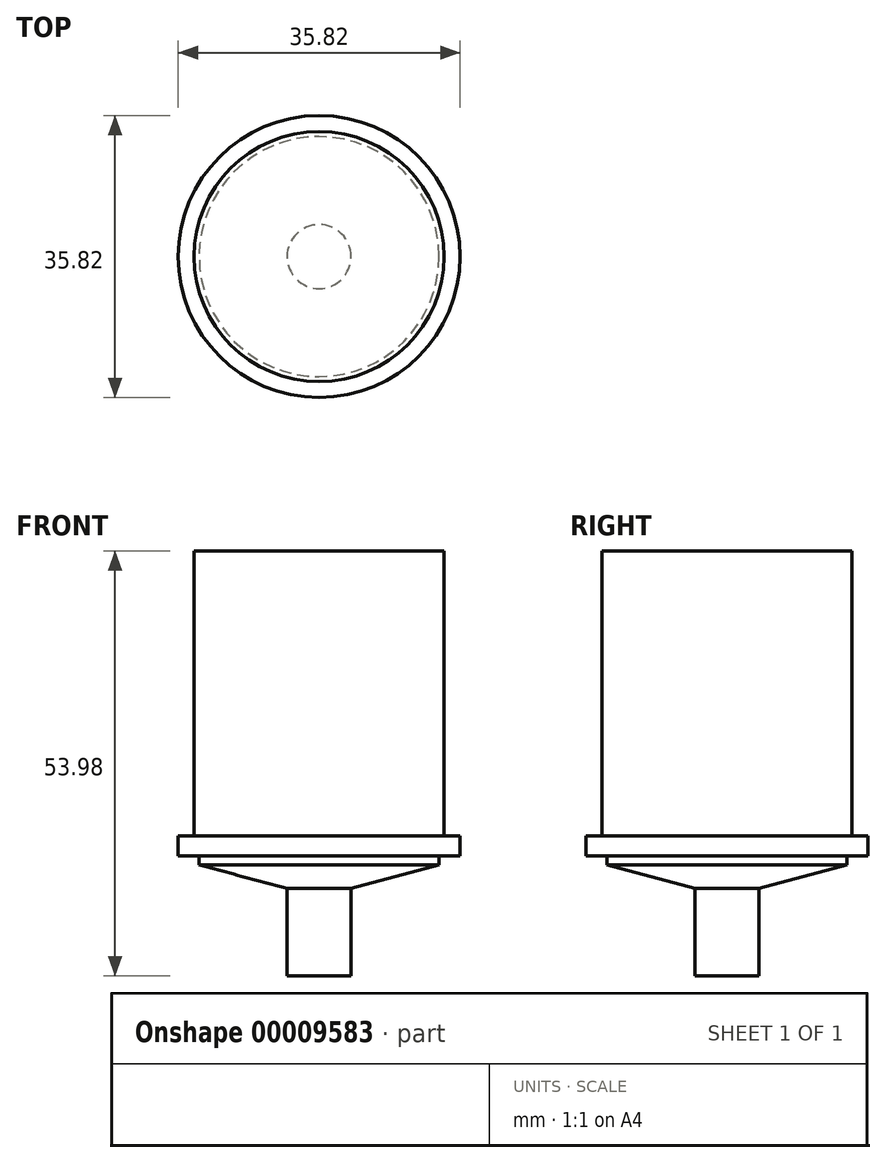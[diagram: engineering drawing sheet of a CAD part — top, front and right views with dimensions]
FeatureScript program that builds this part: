
annotation { "Feature Type Name" : "Feature", "Feature Type Description" : "" }
export const myFeature = defineFeature(function(context is Context, id is Id, definition is map)
    precondition{}
    {
        {
            var Q0;
            Q0=qCreatedBy(makeId("Front.planeOp"),FACE);
            var sketch = newSketch(context, id + "F0", { "sketchPlane" : qUnion([Q0])});
            skLineSegment(sketch, "E0", {"start": v(0, 0) * mm, "end": v(0, 53.98) * mm});
            skLineSegment(sketch, "E1", {"start": v(0, 53.98) * mm, "end": v(-15.88, 53.98) * mm});
            skLineSegment(sketch, "E2", {"start": v(-15.88, 53.97) * mm, "end": v(-15.87, 17.78) * mm});
            skLineSegment(sketch, "E3", {"start": v(-15.87, 17.78) * mm, "end": v(-17.9, 17.78) * mm});
            skLineSegment(sketch, "E4", {"start": v(-17.9, 17.78) * mm, "end": v(-17.9, 15.24) * mm});
            skLineSegment(sketch, "E5", {"start": v(-17.9, 15.24) * mm, "end": v(-15.24, 15.24) * mm});
            skLineSegment(sketch, "E6", {"start": v(-15.24, 15.24) * mm, "end": v(-15.24, 14.1) * mm});
            skLineSegment(sketch, "E7", {"start": v(-15.24, 14.1) * mm, "end": v(-4.06, 11.11) * mm});
            skLineSegment(sketch, "E8", {"start": v(-4.06, 11.11) * mm, "end": v(-4.06, 0) * mm});
            skLineSegment(sketch, "E9", {"start": v(-4.06, 0) * mm, "end": v(0, 0) * mm});
            skSolve(sketch);
        }
        {
            var Q0;
            Q0=qCreatedBy(makeId("Front.planeOp"),FACE);
            var sketch = newSketch(context, id + "F1", { "sketchPlane" : qUnion([Q0])});
            skLineSegment(sketch, "E10", {"start": v(0, 0) * mm, "end": v(0, 63.39) * mm, "construction": true});
            skSolve(sketch);
        }
        {
            var Q0;
            Q0=makeQuery(id+"F0.imprint","IMPRINT",FACE,{"disambiguationData":[TD([[makeQuery(id+"F0.imprint","IMPRINT",EDGE,{"derivedFrom":sQuery(id+"F0.wireOp",EDGE,"E0")}),1.0]])]});
            var Q1;
            Q1=sQuery(id+"F1.wireOp",EDGE,"E10");
            revolve(context, id + "F2", {"entities" : qUnion([Q0]), "axis" : qUnion([Q1]), "revolveType" : RevolveType.FULL});
        }
    });
